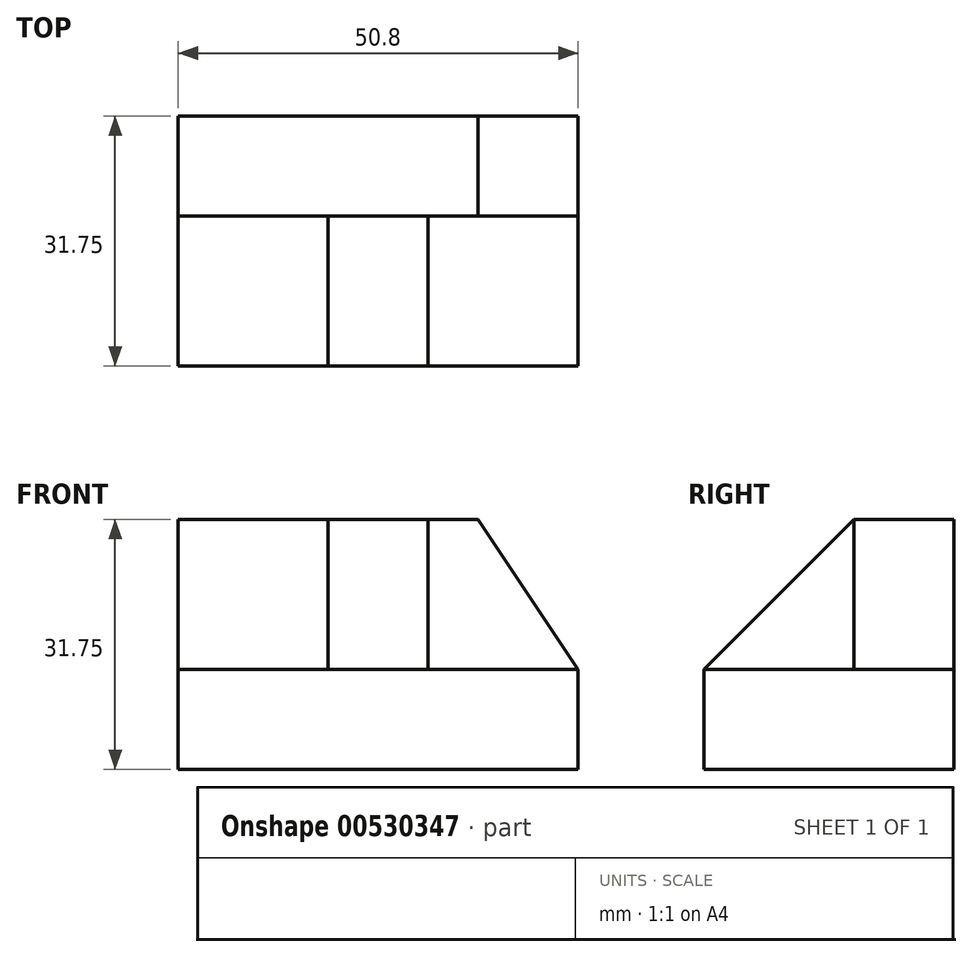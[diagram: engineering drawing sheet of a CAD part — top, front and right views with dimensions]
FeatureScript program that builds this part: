
annotation { "Feature Type Name" : "Feature", "Feature Type Description" : "" }
export const myFeature = defineFeature(function(context is Context, id is Id, definition is map)
    precondition{}
    {
        {
            var Q0;
            Q0=qCreatedBy(makeId("Right.planeOp"),FACE);
            var sketch = newSketch(context, id + "F0", { "sketchPlane" : qUnion([Q0])});
            skLineSegment(sketch, "E0", {"start": v(46.88, 31.75) * mm, "end": v(46.88, 0) * mm});
            skLineSegment(sketch, "E1", {"start": v(46.88, 0) * mm, "end": v(15.13, 0) * mm});
            skLineSegment(sketch, "E2", {"start": v(15.13, 0) * mm, "end": v(15.13, 12.7) * mm});
            skLineSegment(sketch, "E3", {"start": v(15.13, 12.7) * mm, "end": v(34.18, 12.7) * mm});
            skLineSegment(sketch, "E4", {"start": v(34.18, 12.7) * mm, "end": v(34.18, 31.75) * mm});
            skLineSegment(sketch, "E5", {"start": v(34.18, 31.75) * mm, "end": v(46.88, 31.75) * mm});
            skSolve(sketch);
        }
        {
            var Q0;
            Q0 = qSketchRegion(id + "F0", true);
            extrude(context, id + "F1", {"entities" : qUnion([Q0]), "depth" : 50.8 * mm, "offsetDistance" : 25.4 * mm});
        }
        {
            var Q0;
            Q0=makeQuery(id+"F1.opExtrude","SWEPT_FACE",FACE,{"disambiguationData":[OSD([sQuery(id+"F0.wireOp",EDGE,"E4")])]});
            var sketch = newSketch(context, id + "F2", { "sketchPlane" : qUnion([Q0])});
            skLineSegment(sketch, "E6", {"start": v(38.1, 31.75) * mm, "end": v(50.8, 12.7) * mm});
            skSolve(sketch);
        }
        {
            var Q0;
            Q0 = qSketchRegion(id + "F2", true);
            var Q1;
            {var subQ0=sQuery(id+"F2.wireOp",EDGE,"E6");Q1=makeQuery(id+"F2.imprint","IMPRINT",FACE,{"disambiguationData":[TD([[makeQuery(id+"F2.imprint","IMPRINT",EDGE,{"derivedFrom":subQ0}),1.0]])]});}
            extrude(context, id + "F3", {"entities" : qUnion([Q0, Q1]), "operationType" : NewBodyOperationType.REMOVE, "endBound" : BoundingType.THROUGH_ALL, "oppositeDirection" : true, "depth" : 25.4 * mm, "offsetDistance" : 25.4 * mm});
        }
        {
            var Q0;
            Q0=makeQuery(id+"F1.opExtrude","SWEPT_FACE",FACE,{"disambiguationData":[OSD([sQuery(id+"F0.wireOp",EDGE,"E3")])]});
            var sketch = newSketch(context, id + "F4", { "sketchPlane" : qUnion([Q0])});
            skLineSegment(sketch, "E7", {"start": v(19.05, 34.18) * mm, "end": v(19.05, 15.13) * mm});
            skLineSegment(sketch, "E8", {"start": v(31.75, 34.18) * mm, "end": v(31.75, 15.13) * mm});
            skSolve(sketch);
        }
        {
            var Q0;
            Q0 = qSketchRegion(id + "F4", true);
            var Q1;
            {var subQ0=sQuery(id+"F4.wireOp",EDGE,"E7");Q1=makeQuery(id+"F4.imprint","IMPRINT",FACE,{"disambiguationData":[TD([[makeQuery(id+"F4.imprint","IMPRINT",EDGE,{"derivedFrom":subQ0}),1.0]])]});}
            extrude(context, id + "F5", {"entities" : qUnion([Q0, Q1]), "operationType" : NewBodyOperationType.ADD, "depth" : 19.05 * mm, "offsetDistance" : 25.4 * mm});
        }
        {
            var Q0;
            Q0=makeQuery(id+"F5.opExtrude","SWEPT_FACE",FACE,{"disambiguationData":[OSD([sQuery(id+"F4.wireOp",EDGE,"E8")])]});
            var sketch = newSketch(context, id + "F6", { "sketchPlane" : qUnion([Q0])});
            skLineSegment(sketch, "E9", {"start": v(34.18, 31.75) * mm, "end": v(15.13, 12.7) * mm});
            skSolve(sketch);
        }
        {
            var Q0;
            Q0 = qSketchRegion(id + "F6", true);
            var Q1;
            Q1=makeQuery(id+"F6.imprint","IMPRINT",FACE,{"disambiguationData":[TD([[makeQuery(id+"F6.imprint","IMPRINT",EDGE,{"derivedFrom":sQuery(id+"F6.wireOp",EDGE,"E9")}),-1.0]])]});
            extrude(context, id + "F7", {"entities" : qUnion([Q0, Q1]), "operationType" : NewBodyOperationType.REMOVE, "endBound" : BoundingType.THROUGH_ALL, "oppositeDirection" : true, "depth" : 25.4 * mm, "offsetDistance" : 25.4 * mm});
        }
    });
